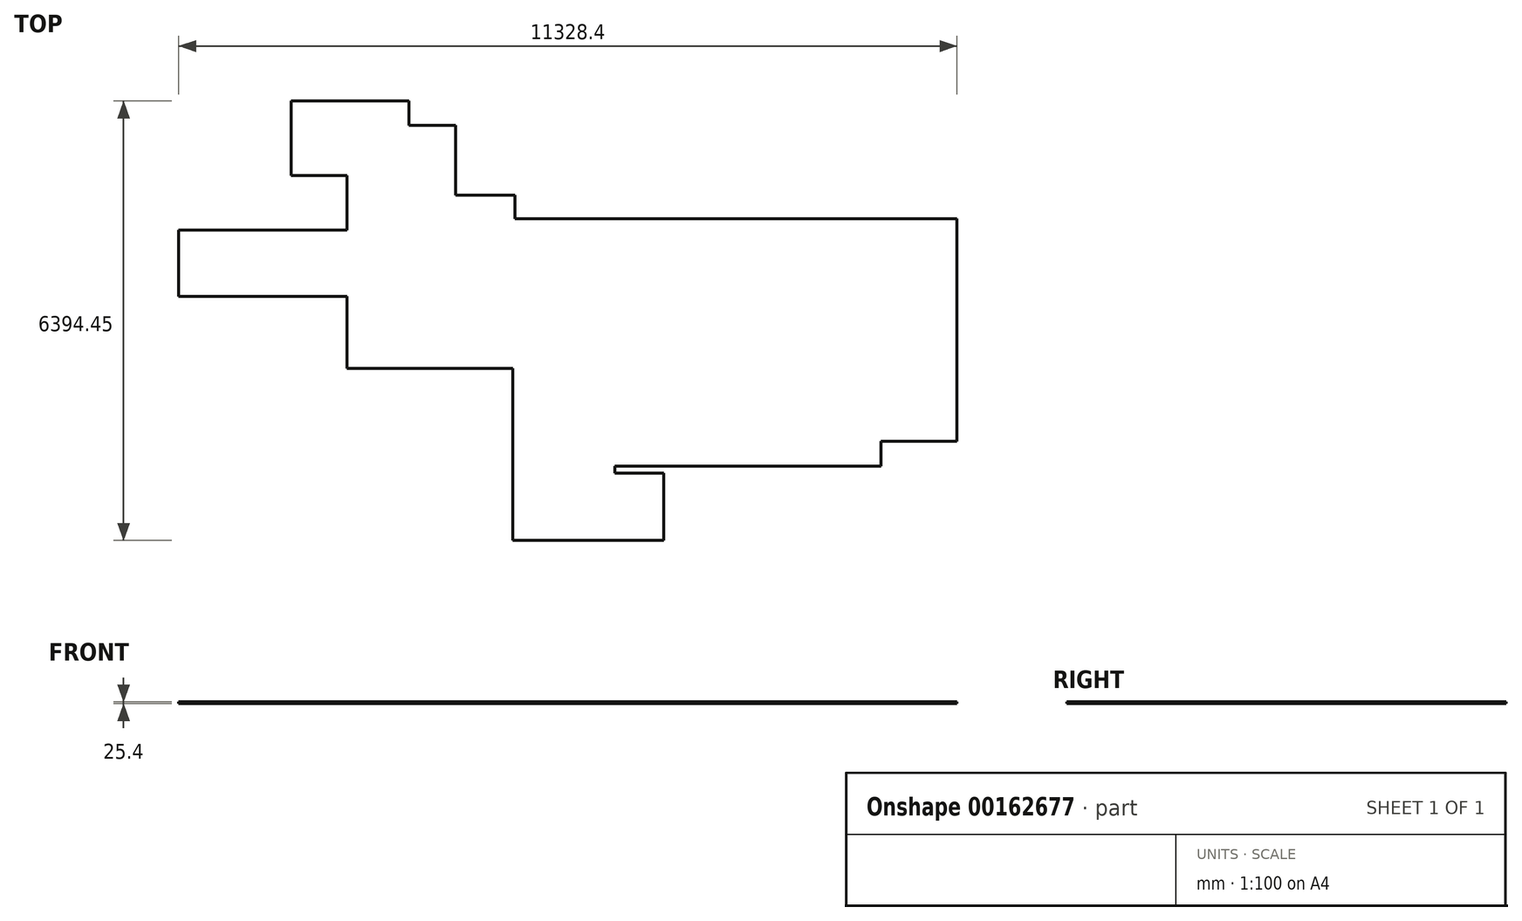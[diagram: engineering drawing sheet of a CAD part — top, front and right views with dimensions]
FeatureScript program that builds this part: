
annotation { "Feature Type Name" : "Feature", "Feature Type Description" : "" }
export const myFeature = defineFeature(function(context is Context, id is Id, definition is map)
    precondition{}
    {
        {
            var Q0;
            Q0=qCreatedBy(makeId("Top.planeOp"),FACE);
            var sketch = newSketch(context, id + "F0", { "sketchPlane" : qUnion([Q0])});
            skLineSegment(sketch, "E0", {"start": v(0, 0) * mm, "end": v(6432.55, 0) * mm});
            skLineSegment(sketch, "E1", {"start": v(6432.55, 0) * mm, "end": v(6432.55, -3238.5) * mm});
            skLineSegment(sketch, "E2", {"start": v(6432.55, -3238.5) * mm, "end": v(5327.65, -3238.5) * mm});
            skLineSegment(sketch, "E3", {"start": v(5327.65, -3238.5) * mm, "end": v(5327.65, -3600.45) * mm});
            skLineSegment(sketch, "E4", {"start": v(5327.65, -3600.45) * mm, "end": v(1454.15, -3600.45) * mm});
            skLineSegment(sketch, "E5", {"start": v(1454.15, -3600.45) * mm, "end": v(1454.15, -3702.05) * mm});
            skLineSegment(sketch, "E6", {"start": v(1454.15, -3702.05) * mm, "end": v(2165.35, -3702.05) * mm});
            skLineSegment(sketch, "E7", {"start": v(2165.35, -3702.05) * mm, "end": v(2165.35, -4679.95) * mm});
            skLineSegment(sketch, "E8", {"start": v(2165.35, -4679.95) * mm, "end": v(-31.75, -4679.95) * mm});
            skLineSegment(sketch, "E9", {"start": v(-31.75, -4679.95) * mm, "end": v(-31.75, -2178.05) * mm});
            skLineSegment(sketch, "E10", {"start": v(-31.75, -2178.05) * mm, "end": v(-2444.75, -2178.05) * mm});
            skLineSegment(sketch, "E11", {"start": v(-2444.75, -2178.05) * mm, "end": v(-2444.75, -1130.3) * mm});
            skLineSegment(sketch, "E12", {"start": v(-2444.75, -1130.3) * mm, "end": v(-4895.85, -1130.3) * mm});
            skLineSegment(sketch, "E13", {"start": v(-4895.85, -1130.3) * mm, "end": v(-4895.85, -165.1) * mm});
            skLineSegment(sketch, "E14", {"start": v(-4895.85, -165.1) * mm, "end": v(-2444.75, -165.1) * mm});
            skLineSegment(sketch, "E15", {"start": v(-2444.75, -165.1) * mm, "end": v(-2444.75, 628.65) * mm});
            skLineSegment(sketch, "E16", {"start": v(-2444.75, 628.65) * mm, "end": v(-3257.55, 628.65) * mm});
            skLineSegment(sketch, "E17", {"start": v(0, 0) * mm, "end": v(0, 342.9) * mm});
            skLineSegment(sketch, "E18", {"start": v(0, 342.9) * mm, "end": v(-863.6, 342.9) * mm});
            skLineSegment(sketch, "E19", {"start": v(-863.6, 342.9) * mm, "end": v(-863.6, 1358.9) * mm});
            skLineSegment(sketch, "E20", {"start": v(-863.6, 1358.9) * mm, "end": v(-1543.05, 1358.9) * mm});
            skLineSegment(sketch, "E21", {"start": v(-1543.05, 1358.9) * mm, "end": v(-1543.05, 1714.5) * mm});
            skLineSegment(sketch, "E22", {"start": v(-1543.05, 1714.5) * mm, "end": v(-3257.55, 1714.5) * mm});
            skLineSegment(sketch, "E23", {"start": v(-3257.55, 628.65) * mm, "end": v(-3257.55, 1714.5) * mm});
            skLineSegment(sketch, "E24", {"start": v(-863.6, 999.92) * mm, "end": v(350.58, 999.92) * mm});
            skLineSegment(sketch, "E25", {"start": v(350.58, 999.92) * mm, "end": v(350.58, 342.9) * mm});
            skLineSegment(sketch, "E26", {"start": v(0, 342.9) * mm, "end": v(350.58, 342.9) * mm});
            skLineSegment(sketch, "E27", {"start": v(2165.35, -3702.05) * mm, "end": v(2293.65, -3702.05) * mm});
            skLineSegment(sketch, "E28", {"start": v(2293.65, -3702.05) * mm, "end": v(5328.95, -3702.05) * mm});
            skLineSegment(sketch, "E29", {"start": v(5328.95, -3702.05) * mm, "end": v(5328.95, -4064) * mm});
            skLineSegment(sketch, "E30", {"start": v(5328.95, -4064) * mm, "end": v(6440.2, -4064) * mm});
            skLineSegment(sketch, "E31", {"start": v(6440.2, -4064) * mm, "end": v(6440.2, -6959.6) * mm});
            skLineSegment(sketch, "E32", {"start": v(6440.2, -6959.6) * mm, "end": v(5805.2, -6959.6) * mm});
            skLineSegment(sketch, "E33", {"start": v(5805.2, -6959.6) * mm, "end": v(5805.2, -7188.2) * mm});
            skLineSegment(sketch, "E34", {"start": v(5805.2, -7188.2) * mm, "end": v(2293.65, -7188.2) * mm});
            skLineSegment(sketch, "E35", {"start": v(2293.65, -7188.2) * mm, "end": v(2293.65, -3702.05) * mm});
            skSolve(sketch);
        }
        {
            var Q0;
            Q0=qCreatedBy(makeId("Top.planeOp"),FACE);
            var sketch = newSketch(context, id + "F1", { "sketchPlane" : qUnion([Q0])});
            skSolve(sketch);
        }
        {
            var Q0;
            Q0 = qSketchRegion(id + "F1", true);
            var Q1;
            Q1=makeQuery(id+"F0.imprint","IMPRINT",FACE,{"disambiguationData":[TD([[makeQuery(id+"F0.imprint","IMPRINT",EDGE,{"derivedFrom":sQuery(id+"F0.wireOp",EDGE,"E0")}),-1.0]])]});
            extrude(context, id + "F2", {"entities" : qUnion([Q0, Q1]), "depth" : 25.4 * mm});
        }
    });
